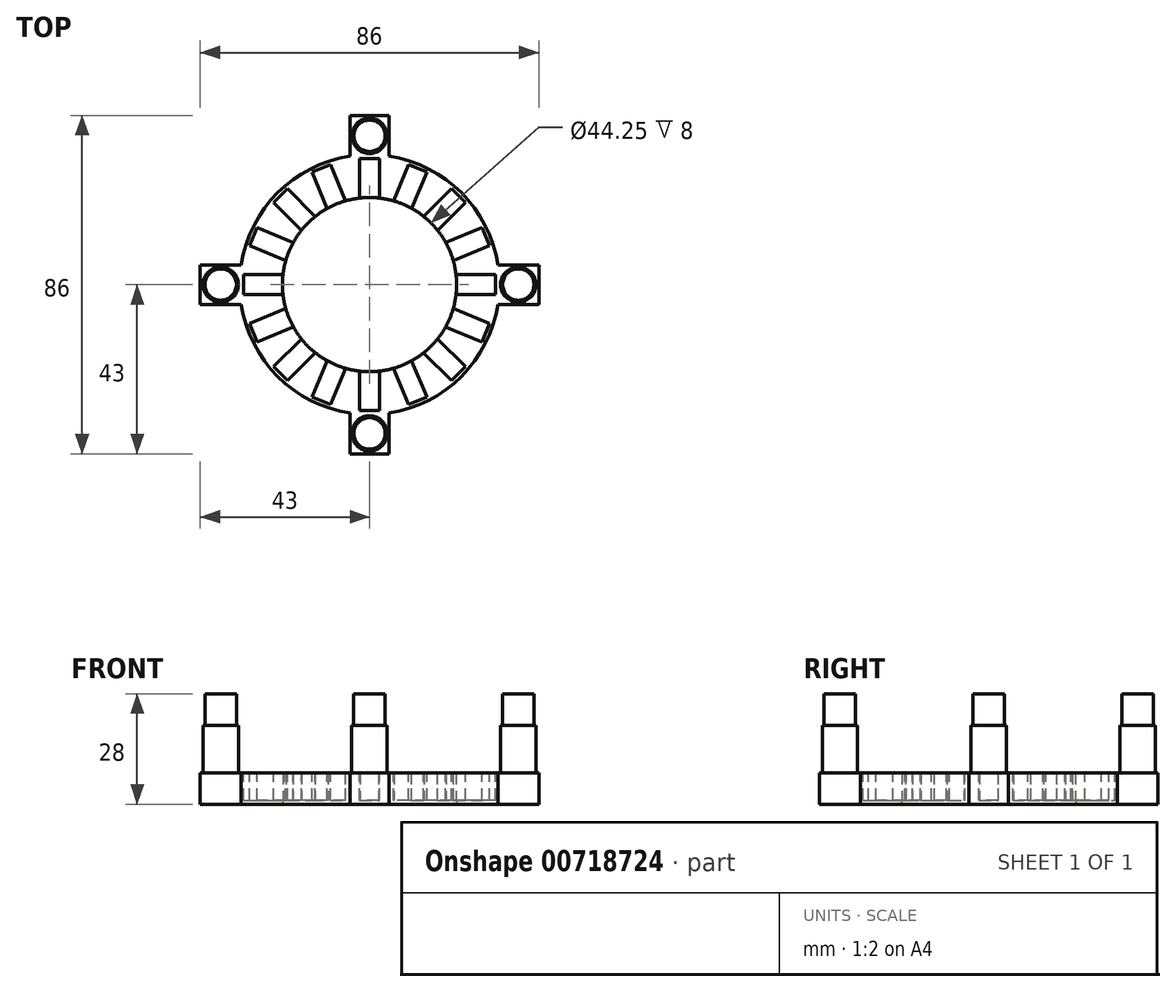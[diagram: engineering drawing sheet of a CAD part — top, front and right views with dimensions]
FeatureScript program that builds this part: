
annotation { "Feature Type Name" : "Feature", "Feature Type Description" : "" }
export const myFeature = defineFeature(function(context is Context, id is Id, definition is map)
    precondition{}
    {
        {
            var Q0;
            Q0=qCreatedBy(makeId("Front.planeOp"),FACE);
            var sketch = newSketch(context, id + "F0", { "sketchPlane" : qUnion([Q0])});
            skLineSegment(sketch, "E0", {"start": v(0, 0) * mm, "end": v(0, 8) * mm});
            skLineSegment(sketch, "E1", {"start": v(0, 8) * mm, "end": v(33, 8) * mm});
            skLineSegment(sketch, "E2", {"start": v(33, 8) * mm, "end": v(33, 0) * mm});
            skLineSegment(sketch, "E3", {"start": v(33, 0) * mm, "end": v(0, 0) * mm});
            skSolve(sketch);
        }
        {
            var Q0;
            Q0=qSketchRegion(id+"F0",true);
            var Q1;
            Q1=sQuery(id+"F0.wireOp",EDGE,"E0");
            revolve(context, id + "F1", {"surfaceOperationType" : NewSurfaceOperationType.NEW, "entities" : qUnion([Q0]), "axis" : qUnion([Q1]), "revolveType" : RevolveType.FULL});
        }
        {
            var Q0;
            Q0=qCreatedBy(makeId("Top.planeOp"),FACE);
            var sketch = newSketch(context, id + "F2", { "sketchPlane" : qUnion([Q0])});
            skCircle(sketch, "E4", {"center": v(0, 0) * mm, "radius": 22.12 * mm});
            skSolve(sketch);
        }
        {
            var Q0;
            Q0=qSketchRegion(id+"F2",true);
            extrude(context, id + "F3", {"entities" : qUnion([Q0]), "operationType" : NewBodyOperationType.REMOVE, "depth" : 25 * mm, "offsetDistance" : 25 * mm});
        }
        {
            var Q0;
            Q0=makeQuery(id+"F1.opRevolve","SWEPT_FACE",FACE,{"disambiguationData":[OSD([sQuery(id+"F0.wireOp",EDGE,"E1")])]});
            var sketch = newSketch(context, id + "F4", { "sketchPlane" : qUnion([Q0])});
            skLineSegment(sketch, "E5", {"start": v(0, 0) * mm, "end": v(0, 22) * mm});
            skLineSegment(sketch, "E6", {"start": v(0, 22) * mm, "end": v(-2.5, 22) * mm});
            skLineSegment(sketch, "E7", {"start": v(-2.5, 22) * mm, "end": v(-2.5, 32) * mm});
            skLineSegment(sketch, "E8", {"start": v(-2.5, 32) * mm, "end": v(2.5, 32) * mm});
            skLineSegment(sketch, "E9", {"start": v(2.5, 32) * mm, "end": v(2.5, 22) * mm});
            skLineSegment(sketch, "E10", {"start": v(2.5, 22) * mm, "end": v(0, 22) * mm});
            skLineSegment(sketch, "E11.1.0", {"start": v(-10.73, 19.37) * mm, "end": v(-14.56, 28.6) * mm});
            skLineSegment(sketch, "E11.1.1", {"start": v(-14.56, 28.6) * mm, "end": v(-9.94, 30.52) * mm});
            skLineSegment(sketch, "E11.1.2", {"start": v(-9.94, 30.52) * mm, "end": v(-6.1, 21.28) * mm});
            skLineSegment(sketch, "E11.1.3", {"start": v(-6.1, 21.28) * mm, "end": v(-8.42, 20.33) * mm});
            skLineSegment(sketch, "E11.1.4", {"start": v(-8.42, 20.33) * mm, "end": v(-10.73, 19.37) * mm});
            skLineSegment(sketch, "E11.2.0", {"start": v(-17.32, 13.79) * mm, "end": v(-24.4, 20.86) * mm});
            skLineSegment(sketch, "E11.2.1", {"start": v(-24.4, 20.86) * mm, "end": v(-20.86, 24.4) * mm});
            skLineSegment(sketch, "E11.2.2", {"start": v(-20.86, 24.4) * mm, "end": v(-13.79, 17.32) * mm});
            skLineSegment(sketch, "E11.2.3", {"start": v(-13.79, 17.32) * mm, "end": v(-15.56, 15.56) * mm});
            skLineSegment(sketch, "E11.2.4", {"start": v(-15.56, 15.56) * mm, "end": v(-17.32, 13.79) * mm});
            skPoint(sketch, "E11.center", {"position": v(0, 0) * mm});
            skLineSegment(sketch, "E12.1.3.0", {"start": v(-21.28, 6.1) * mm, "end": v(-30.52, 9.94) * mm});
            skLineSegment(sketch, "E12.3.3.0", {"start": v(-30.52, 9.94) * mm, "end": v(-28.6, 14.56) * mm});
            skLineSegment(sketch, "E12.6.3.0", {"start": v(-28.6, 14.56) * mm, "end": v(-19.37, 10.73) * mm});
            skLineSegment(sketch, "E12.9.3.0", {"start": v(-19.37, 10.73) * mm, "end": v(-20.33, 8.42) * mm});
            skLineSegment(sketch, "E12.12.3.0", {"start": v(-20.33, 8.42) * mm, "end": v(-21.28, 6.1) * mm});
            skLineSegment(sketch, "E12.1.4.0", {"start": v(-22, -2.5) * mm, "end": v(-32, -2.5) * mm});
            skLineSegment(sketch, "E12.3.4.0", {"start": v(-32, -2.5) * mm, "end": v(-32, 2.5) * mm});
            skLineSegment(sketch, "E12.6.4.0", {"start": v(-32, 2.5) * mm, "end": v(-22, 2.5) * mm});
            skLineSegment(sketch, "E12.9.4.0", {"start": v(-22, 2.5) * mm, "end": v(-22, 0) * mm});
            skLineSegment(sketch, "E12.12.4.0", {"start": v(-22, 0) * mm, "end": v(-22, -2.5) * mm});
            skLineSegment(sketch, "E12.1.5.0", {"start": v(-19.37, -10.73) * mm, "end": v(-28.6, -14.56) * mm});
            skLineSegment(sketch, "E12.3.5.0", {"start": v(-28.6, -14.56) * mm, "end": v(-30.52, -9.94) * mm});
            skLineSegment(sketch, "E12.6.5.0", {"start": v(-30.52, -9.94) * mm, "end": v(-21.28, -6.1) * mm});
            skLineSegment(sketch, "E12.9.5.0", {"start": v(-21.28, -6.1) * mm, "end": v(-20.33, -8.42) * mm});
            skLineSegment(sketch, "E12.12.5.0", {"start": v(-20.33, -8.42) * mm, "end": v(-19.37, -10.73) * mm});
            skLineSegment(sketch, "E12.1.6.0", {"start": v(-13.79, -17.32) * mm, "end": v(-20.86, -24.4) * mm});
            skLineSegment(sketch, "E12.3.6.0", {"start": v(-20.86, -24.4) * mm, "end": v(-24.4, -20.86) * mm});
            skLineSegment(sketch, "E12.6.6.0", {"start": v(-24.4, -20.86) * mm, "end": v(-17.32, -13.79) * mm});
            skLineSegment(sketch, "E12.9.6.0", {"start": v(-17.32, -13.79) * mm, "end": v(-15.56, -15.56) * mm});
            skLineSegment(sketch, "E12.12.6.0", {"start": v(-15.56, -15.56) * mm, "end": v(-13.79, -17.32) * mm});
            skLineSegment(sketch, "E12.1.7.0", {"start": v(-6.1, -21.28) * mm, "end": v(-9.94, -30.52) * mm});
            skLineSegment(sketch, "E12.3.7.0", {"start": v(-9.94, -30.52) * mm, "end": v(-14.56, -28.6) * mm});
            skLineSegment(sketch, "E12.6.7.0", {"start": v(-14.56, -28.6) * mm, "end": v(-10.73, -19.37) * mm});
            skLineSegment(sketch, "E12.9.7.0", {"start": v(-10.73, -19.37) * mm, "end": v(-8.42, -20.33) * mm});
            skLineSegment(sketch, "E12.12.7.0", {"start": v(-8.42, -20.33) * mm, "end": v(-6.1, -21.28) * mm});
            skLineSegment(sketch, "E12.1.8.0", {"start": v(2.5, -22) * mm, "end": v(2.5, -32) * mm});
            skLineSegment(sketch, "E12.3.8.0", {"start": v(2.5, -32) * mm, "end": v(-2.5, -32) * mm});
            skLineSegment(sketch, "E12.6.8.0", {"start": v(-2.5, -32) * mm, "end": v(-2.5, -22) * mm});
            skLineSegment(sketch, "E12.9.8.0", {"start": v(-2.5, -22) * mm, "end": v(0, -22) * mm});
            skLineSegment(sketch, "E12.12.8.0", {"start": v(0, -22) * mm, "end": v(2.5, -22) * mm});
            skLineSegment(sketch, "E12.1.9.0", {"start": v(10.73, -19.37) * mm, "end": v(14.56, -28.6) * mm});
            skLineSegment(sketch, "E12.3.9.0", {"start": v(14.56, -28.6) * mm, "end": v(9.94, -30.52) * mm});
            skLineSegment(sketch, "E12.6.9.0", {"start": v(9.94, -30.52) * mm, "end": v(6.1, -21.28) * mm});
            skLineSegment(sketch, "E12.9.9.0", {"start": v(6.1, -21.28) * mm, "end": v(8.42, -20.33) * mm});
            skLineSegment(sketch, "E12.12.9.0", {"start": v(8.42, -20.33) * mm, "end": v(10.73, -19.37) * mm});
            skLineSegment(sketch, "E12.1.10.0", {"start": v(17.32, -13.79) * mm, "end": v(24.4, -20.86) * mm});
            skLineSegment(sketch, "E12.3.10.0", {"start": v(24.4, -20.86) * mm, "end": v(20.86, -24.4) * mm});
            skLineSegment(sketch, "E12.6.10.0", {"start": v(20.86, -24.4) * mm, "end": v(13.79, -17.32) * mm});
            skLineSegment(sketch, "E12.9.10.0", {"start": v(13.79, -17.32) * mm, "end": v(15.56, -15.56) * mm});
            skLineSegment(sketch, "E12.12.10.0", {"start": v(15.56, -15.56) * mm, "end": v(17.32, -13.79) * mm});
            skLineSegment(sketch, "E12.1.11.0", {"start": v(21.28, -6.1) * mm, "end": v(30.52, -9.94) * mm});
            skLineSegment(sketch, "E12.3.11.0", {"start": v(30.52, -9.94) * mm, "end": v(28.6, -14.56) * mm});
            skLineSegment(sketch, "E12.6.11.0", {"start": v(28.6, -14.56) * mm, "end": v(19.37, -10.73) * mm});
            skLineSegment(sketch, "E12.9.11.0", {"start": v(19.37, -10.73) * mm, "end": v(20.33, -8.42) * mm});
            skLineSegment(sketch, "E12.12.11.0", {"start": v(20.33, -8.42) * mm, "end": v(21.28, -6.1) * mm});
            skLineSegment(sketch, "E12.1.12.0", {"start": v(22, 2.5) * mm, "end": v(32, 2.5) * mm});
            skLineSegment(sketch, "E12.3.12.0", {"start": v(32, 2.5) * mm, "end": v(32, -2.5) * mm});
            skLineSegment(sketch, "E12.6.12.0", {"start": v(32, -2.5) * mm, "end": v(22, -2.5) * mm});
            skLineSegment(sketch, "E12.9.12.0", {"start": v(22, -2.5) * mm, "end": v(22, 0) * mm});
            skLineSegment(sketch, "E12.12.12.0", {"start": v(22, 0) * mm, "end": v(22, 2.5) * mm});
            skLineSegment(sketch, "E12.1.13.0", {"start": v(19.37, 10.73) * mm, "end": v(28.6, 14.56) * mm});
            skLineSegment(sketch, "E12.3.13.0", {"start": v(28.6, 14.56) * mm, "end": v(30.52, 9.94) * mm});
            skLineSegment(sketch, "E12.6.13.0", {"start": v(30.52, 9.94) * mm, "end": v(21.28, 6.1) * mm});
            skLineSegment(sketch, "E12.9.13.0", {"start": v(21.28, 6.1) * mm, "end": v(20.33, 8.42) * mm});
            skLineSegment(sketch, "E12.12.13.0", {"start": v(20.33, 8.42) * mm, "end": v(19.37, 10.73) * mm});
            skLineSegment(sketch, "E12.1.14.0", {"start": v(13.79, 17.32) * mm, "end": v(20.86, 24.4) * mm});
            skLineSegment(sketch, "E12.3.14.0", {"start": v(20.86, 24.4) * mm, "end": v(24.4, 20.86) * mm});
            skLineSegment(sketch, "E12.6.14.0", {"start": v(24.4, 20.86) * mm, "end": v(17.32, 13.79) * mm});
            skLineSegment(sketch, "E12.9.14.0", {"start": v(17.32, 13.79) * mm, "end": v(15.56, 15.56) * mm});
            skLineSegment(sketch, "E12.12.14.0", {"start": v(15.56, 15.56) * mm, "end": v(13.79, 17.32) * mm});
            skLineSegment(sketch, "E12.1.15.0", {"start": v(6.1, 21.28) * mm, "end": v(9.94, 30.52) * mm});
            skLineSegment(sketch, "E12.3.15.0", {"start": v(9.94, 30.52) * mm, "end": v(14.56, 28.6) * mm});
            skLineSegment(sketch, "E12.6.15.0", {"start": v(14.56, 28.6) * mm, "end": v(10.73, 19.37) * mm});
            skLineSegment(sketch, "E12.9.15.0", {"start": v(10.73, 19.37) * mm, "end": v(8.42, 20.33) * mm});
            skLineSegment(sketch, "E12.12.15.0", {"start": v(8.42, 20.33) * mm, "end": v(6.1, 21.28) * mm});
            skSolve(sketch);
        }
        {
            var Q0;
            Q0=qSketchRegion(id+"F4",true);
            extrude(context, id + "F5", {"entities" : qUnion([Q0]), "operationType" : NewBodyOperationType.REMOVE, "oppositeDirection" : true, "depth" : 7 * mm, "offsetDistance" : 25 * mm});
        }
        {
            var Q0;
            Q0=qCreatedBy(makeId("Top.planeOp"),FACE);
            var sketch = newSketch(context, id + "F6", { "sketchPlane" : qUnion([Q0])});
            skLineSegment(sketch, "E13", {"start": v(0, 0) * mm, "end": v(0, 8) * mm});
            skLineSegment(sketch, "E14", {"start": v(43, 0) * mm, "end": v(43, -5) * mm});
            skLineSegment(sketch, "E15", {"start": v(43, -5) * mm, "end": v(32.62, -5) * mm});
            skLineSegment(sketch, "E16", {"start": v(43, 0) * mm, "end": v(43, 5) * mm});
            skLineSegment(sketch, "E17", {"start": v(43, 5) * mm, "end": v(32.62, 5) * mm});
            skLineSegment(sketch, "E18.1.0", {"start": v(5, 43) * mm, "end": v(5, 32.62) * mm});
            skLineSegment(sketch, "E18.1.1", {"start": v(0, 43) * mm, "end": v(5, 43) * mm});
            skLineSegment(sketch, "E18.1.2", {"start": v(0, 43) * mm, "end": v(-5, 43) * mm});
            skLineSegment(sketch, "E18.1.3", {"start": v(-5, 43) * mm, "end": v(-5, 32.62) * mm});
            skLineSegment(sketch, "E18.2.0", {"start": v(-43, 5) * mm, "end": v(-32.62, 5) * mm});
            skLineSegment(sketch, "E18.2.1", {"start": v(-43, 0) * mm, "end": v(-43, 5) * mm});
            skLineSegment(sketch, "E18.2.2", {"start": v(-43, 0) * mm, "end": v(-43, -5) * mm});
            skLineSegment(sketch, "E18.2.3", {"start": v(-43, -5) * mm, "end": v(-32.62, -5) * mm});
            skLineSegment(sketch, "E18.3.0", {"start": v(-5, -43) * mm, "end": v(-5, -32.62) * mm});
            skLineSegment(sketch, "E18.3.1", {"start": v(0, -43) * mm, "end": v(-5, -43) * mm});
            skLineSegment(sketch, "E18.3.2", {"start": v(0, -43) * mm, "end": v(5, -43) * mm});
            skLineSegment(sketch, "E18.3.3", {"start": v(5, -43) * mm, "end": v(5, -32.62) * mm});
            skPoint(sketch, "E18.center", {"position": v(0, 0) * mm});
            skLineSegment(sketch, "E19", {"start": v(32.62, 5) * mm, "end": v(32.62, -5) * mm});
            skLineSegment(sketch, "E20", {"start": v(5, 32.62) * mm, "end": v(-5, 32.62) * mm});
            skLineSegment(sketch, "E21", {"start": v(-32.62, 5) * mm, "end": v(-32.62, -5) * mm});
            skLineSegment(sketch, "E22", {"start": v(-5, -32.62) * mm, "end": v(5, -32.62) * mm});
            skSolve(sketch);
        }
        {
            var Q0;
            Q0=qSketchRegion(id+"F6",true);
            extrude(context, id + "F7", {"entities" : qUnion([Q0]), "operationType" : NewBodyOperationType.ADD, "depth" : 8 * mm, "offsetDistance" : 25 * mm});
        }
        {
            var Q0;
            Q0=makeQuery(id+"F7.boolean.opBoolean","MERGE",FACE,{"derivedFrom":[makeQuery(id+"F1.opRevolve","SWEPT_FACE",FACE,{"disambiguationData":[OSD([sQuery(id+"F0.wireOp",EDGE,"E1")])]}),makeQuery(id+"F7.opExtrude","CAP_FACE",FACE,{"disambiguationData":[OSD([sQuery(id+"F6.wireOp",EDGE,"E14"),sQuery(id+"F6.wireOp",EDGE,"E15"),sQuery(id+"F6.wireOp",EDGE,"E16"),sQuery(id+"F6.wireOp",EDGE,"E17"),sQuery(id+"F6.wireOp",EDGE,"E19")])],"isStart":false}),makeQuery(id+"F7.opExtrude","CAP_FACE",FACE,{"disambiguationData":[OSD([sQuery(id+"F6.wireOp",EDGE,"E18.1.0"),sQuery(id+"F6.wireOp",EDGE,"E18.1.1"),sQuery(id+"F6.wireOp",EDGE,"E18.1.2"),sQuery(id+"F6.wireOp",EDGE,"E18.1.3"),sQuery(id+"F6.wireOp",EDGE,"E20")])],"isStart":false}),makeQuery(id+"F7.opExtrude","CAP_FACE",FACE,{"disambiguationData":[OSD([sQuery(id+"F6.wireOp",EDGE,"E18.2.0"),sQuery(id+"F6.wireOp",EDGE,"E18.2.1"),sQuery(id+"F6.wireOp",EDGE,"E18.2.2"),sQuery(id+"F6.wireOp",EDGE,"E18.2.3"),sQuery(id+"F6.wireOp",EDGE,"E21")])],"isStart":false}),makeQuery(id+"F7.opExtrude","CAP_FACE",FACE,{"disambiguationData":[OSD([sQuery(id+"F6.wireOp",EDGE,"E18.3.0"),sQuery(id+"F6.wireOp",EDGE,"E18.3.1"),sQuery(id+"F6.wireOp",EDGE,"E18.3.2"),sQuery(id+"F6.wireOp",EDGE,"E18.3.3"),sQuery(id+"F6.wireOp",EDGE,"E22")])],"isStart":false})]});
            var sketch = newSketch(context, id + "F8", { "sketchPlane" : qUnion([Q0])});
            skPoint(sketch, "E23", {"position": v(0, 38.1) * mm});
            skPoint(sketch, "E24", {"position": v(37.8, 0) * mm});
            skPoint(sketch, "E24.positionSnap0", {"position": v(37.8, 5) * mm});
            skCircle(sketch, "E25", {"center": v(37.8, 0) * mm, "radius": 4 * mm});
            skCircle(sketch, "E26.1.0", {"center": v(0, 37.8) * mm, "radius": 4 * mm});
            skCircle(sketch, "E26.2.0", {"center": v(-37.8, 0) * mm, "radius": 4 * mm});
            skCircle(sketch, "E26.3.0", {"center": v(0, -37.8) * mm, "radius": 4 * mm});
            skPoint(sketch, "E26.center", {"position": v(0, 0) * mm});
            skSolve(sketch);
        }
        {
            var Q0;
            Q0=makeQuery(id+"F8.imprint","IMPRINT",FACE,{"disambiguationData":[TD([[makeQuery(id+"F8.imprint","IMPRINT",EDGE,{"derivedFrom":sQuery(id+"F8.wireOp",EDGE,"E26.1.0")}),1.0]])]});
            var Q1;
            Q1=makeQuery(id+"F8.imprint","IMPRINT",FACE,{"disambiguationData":[TD([[makeQuery(id+"F8.imprint","IMPRINT",EDGE,{"derivedFrom":sQuery(id+"F8.wireOp",EDGE,"E25")}),1.0]])]});
            var Q2;
            Q2=makeQuery(id+"F8.imprint","IMPRINT",FACE,{"disambiguationData":[TD([[makeQuery(id+"F8.imprint","IMPRINT",EDGE,{"derivedFrom":sQuery(id+"F8.wireOp",EDGE,"E26.2.0")}),1.0]])]});
            var Q3;
            Q3=makeQuery(id+"F8.imprint","IMPRINT",FACE,{"disambiguationData":[TD([[makeQuery(id+"F8.imprint","IMPRINT",EDGE,{"derivedFrom":sQuery(id+"F8.wireOp",EDGE,"E26.3.0")}),1.0]])]});
            extrude(context, id + "F9", {"entities" : qUnion([Q0, Q1, Q2, Q3]), "operationType" : NewBodyOperationType.REMOVE, "oppositeDirection" : true, "depth" : 25 * mm, "offsetDistance" : 25 * mm});
        }
        {
            var Q0;
            Q0=makeQuery(id+"F7.boolean.opBoolean","MERGE",FACE,{"derivedFrom":[makeQuery(id+"F1.opRevolve","SWEPT_FACE",FACE,{"disambiguationData":[OSD([sQuery(id+"F0.wireOp",EDGE,"E3")])]}),makeQuery(id+"F7.opExtrude","CAP_FACE",FACE,{"disambiguationData":[OSD([sQuery(id+"F6.wireOp",EDGE,"E14"),sQuery(id+"F6.wireOp",EDGE,"E15"),sQuery(id+"F6.wireOp",EDGE,"E16"),sQuery(id+"F6.wireOp",EDGE,"E17"),sQuery(id+"F6.wireOp",EDGE,"E19")])],"isStart":true}),makeQuery(id+"F7.opExtrude","CAP_FACE",FACE,{"disambiguationData":[OSD([sQuery(id+"F6.wireOp",EDGE,"E18.1.0"),sQuery(id+"F6.wireOp",EDGE,"E18.1.1"),sQuery(id+"F6.wireOp",EDGE,"E18.1.2"),sQuery(id+"F6.wireOp",EDGE,"E18.1.3"),sQuery(id+"F6.wireOp",EDGE,"E20")])],"isStart":true}),makeQuery(id+"F7.opExtrude","CAP_FACE",FACE,{"disambiguationData":[OSD([sQuery(id+"F6.wireOp",EDGE,"E18.2.0"),sQuery(id+"F6.wireOp",EDGE,"E18.2.1"),sQuery(id+"F6.wireOp",EDGE,"E18.2.2"),sQuery(id+"F6.wireOp",EDGE,"E18.2.3"),sQuery(id+"F6.wireOp",EDGE,"E21")])],"isStart":true}),makeQuery(id+"F7.opExtrude","CAP_FACE",FACE,{"disambiguationData":[OSD([sQuery(id+"F6.wireOp",EDGE,"E18.3.0"),sQuery(id+"F6.wireOp",EDGE,"E18.3.1"),sQuery(id+"F6.wireOp",EDGE,"E18.3.2"),sQuery(id+"F6.wireOp",EDGE,"E18.3.3"),sQuery(id+"F6.wireOp",EDGE,"E22")])],"isStart":true})]});
            var sketch = newSketch(context, id + "F10", { "sketchPlane" : qUnion([Q0])});
            skLineSegment(sketch, "E27", {"start": v(0, -37.8) * mm, "end": v(0, 37.8) * mm});
            skLineSegment(sketch, "E28", {"start": v(37.8, 0) * mm, "end": v(-37.8, 0) * mm});
            skLineSegment(sketch, "E29", {"start": v(0, 37.8) * mm, "end": v(0, 43) * mm});
            skLineSegment(sketch, "E30", {"start": v(0, -37.8) * mm, "end": v(0, -43) * mm});
            skPoint(sketch, "E31", {"position": v(0, 22.12) * mm});
            skPoint(sketch, "E32", {"position": v(0, -22.12) * mm});
            skCircle(sketch, "E33", {"center": v(0, -37.8) * mm, "radius": 4.5 * mm});
            skCircle(sketch, "E34.1.0", {"center": v(37.8, 0) * mm, "radius": 4.5 * mm});
            skCircle(sketch, "E34.2.0", {"center": v(0, 37.8) * mm, "radius": 4.5 * mm});
            skCircle(sketch, "E34.3.0", {"center": v(-37.8, 0) * mm, "radius": 4.5 * mm});
            skPoint(sketch, "E34.center", {"position": v(0, 0) * mm});
            skSolve(sketch);
        }
        {
            var Q0;
            {var subQ0=sQuery(id+"F10.wireOp",EDGE,"E30");var subQ1=sQuery(id+"F10.wireOp",EDGE,"E27");var subQ2=makeQuery(id+"F10.imprint","INTERSECT",VERTEX,{"derivedFrom":[subQ1,subQ0]});Q0=makeQuery(id+"F10.imprint","IMPRINT",FACE,{"disambiguationData":[TD([[makeQuery(id+"F10.imprint","IMPRINT",EDGE,{"disambiguationData":[TD([[subQ2,-1.0]])],"derivedFrom":subQ1}),1.0]])]});}
            var Q1;
            {var subQ0=sQuery(id+"F10.wireOp",EDGE,"E30");var subQ1=sQuery(id+"F10.wireOp",EDGE,"E27");var subQ2=makeQuery(id+"F10.imprint","INTERSECT",VERTEX,{"derivedFrom":[subQ1,subQ0]});Q1=makeQuery(id+"F10.imprint","IMPRINT",FACE,{"disambiguationData":[TD([[makeQuery(id+"F10.imprint","IMPRINT",EDGE,{"disambiguationData":[TD([[subQ2,-1.0]])],"derivedFrom":subQ1}),-1.0]])]});}
            var Q2;
            Q2=makeQuery(id+"F10.imprint","IMPRINT",FACE,{"disambiguationData":[TD([[makeQuery(id+"F10.imprint","IMPRINT",EDGE,{"derivedFrom":makeQuery(id+"F9.boolean.opBoolean","INTERSECT",EDGE,{"derivedFrom":[makeQuery(id+"F7.boolean.opBoolean","MERGE",FACE,{"derivedFrom":[makeQuery(id+"F1.opRevolve","SWEPT_FACE",FACE,{"disambiguationData":[OSD([sQuery(id+"F0.wireOp",EDGE,"E3")])]}),makeQuery(id+"F7.opExtrude","CAP_FACE",FACE,{"disambiguationData":[OSD([sQuery(id+"F6.wireOp",EDGE,"E14"),sQuery(id+"F6.wireOp",EDGE,"E15"),sQuery(id+"F6.wireOp",EDGE,"E16"),sQuery(id+"F6.wireOp",EDGE,"E17"),sQuery(id+"F6.wireOp",EDGE,"E19")])],"isStart":true}),makeQuery(id+"F7.opExtrude","CAP_FACE",FACE,{"disambiguationData":[OSD([sQuery(id+"F6.wireOp",EDGE,"E18.1.0"),sQuery(id+"F6.wireOp",EDGE,"E18.1.1"),sQuery(id+"F6.wireOp",EDGE,"E18.1.2"),sQuery(id+"F6.wireOp",EDGE,"E18.1.3"),sQuery(id+"F6.wireOp",EDGE,"E20")])],"isStart":true}),makeQuery(id+"F7.opExtrude","CAP_FACE",FACE,{"disambiguationData":[OSD([sQuery(id+"F6.wireOp",EDGE,"E18.2.0"),sQuery(id+"F6.wireOp",EDGE,"E18.2.1"),sQuery(id+"F6.wireOp",EDGE,"E18.2.2"),sQuery(id+"F6.wireOp",EDGE,"E18.2.3"),sQuery(id+"F6.wireOp",EDGE,"E21")])],"isStart":true}),makeQuery(id+"F7.opExtrude","CAP_FACE",FACE,{"disambiguationData":[OSD([sQuery(id+"F6.wireOp",EDGE,"E18.3.0"),sQuery(id+"F6.wireOp",EDGE,"E18.3.1"),sQuery(id+"F6.wireOp",EDGE,"E18.3.2"),sQuery(id+"F6.wireOp",EDGE,"E18.3.3"),sQuery(id+"F6.wireOp",EDGE,"E22")])],"isStart":true})]}),makeQuery(id+"F9.opExtrude","SWEPT_FACE",FACE,{"disambiguationData":[OSD([sQuery(id+"F8.wireOp",EDGE,"E25")])]})]})}),-1.0]])]});
            var Q3;
            {var subQ0=sQuery(id+"F10.wireOp",EDGE,"E29");var subQ1=sQuery(id+"F10.wireOp",EDGE,"E27");var subQ2=makeQuery(id+"F10.imprint","INTERSECT",VERTEX,{"derivedFrom":[subQ1,subQ0]});Q3=makeQuery(id+"F10.imprint","IMPRINT",FACE,{"disambiguationData":[TD([[makeQuery(id+"F10.imprint","IMPRINT",EDGE,{"disambiguationData":[TD([[subQ2,1.0]])],"derivedFrom":subQ1}),1.0]])]});}
            var Q4;
            {var subQ0=sQuery(id+"F10.wireOp",EDGE,"E29");var subQ1=sQuery(id+"F10.wireOp",EDGE,"E27");var subQ2=makeQuery(id+"F10.imprint","INTERSECT",VERTEX,{"derivedFrom":[subQ1,subQ0]});Q4=makeQuery(id+"F10.imprint","IMPRINT",FACE,{"disambiguationData":[TD([[makeQuery(id+"F10.imprint","IMPRINT",EDGE,{"disambiguationData":[TD([[subQ2,1.0]])],"derivedFrom":subQ1}),-1.0]])]});}
            var Q5;
            Q5=makeQuery(id+"F10.imprint","IMPRINT",FACE,{"disambiguationData":[TD([[makeQuery(id+"F10.imprint","IMPRINT",EDGE,{"derivedFrom":sQuery(id+"F10.wireOp",EDGE,"E34.1.0")}),1.0]])]});
            var Q6;
            {var subQ0=sQuery(id+"F10.wireOp",EDGE,"E33");var subQ1=sQuery(id+"F10.wireOp",EDGE,"E27");var subQ2=makeQuery(id+"F10.imprint","INTERSECT",VERTEX,{"derivedFrom":[subQ1,subQ0]});Q6=makeQuery(id+"F10.imprint","IMPRINT",FACE,{"disambiguationData":[TD([[makeQuery(id+"F10.imprint","IMPRINT",EDGE,{"disambiguationData":[TD([[subQ2,1.0]])],"derivedFrom":subQ0}),1.0]])]});}
            var Q7;
            {var subQ0=sQuery(id+"F10.wireOp",EDGE,"E33");var subQ1=sQuery(id+"F10.wireOp",EDGE,"E27");var subQ2=makeQuery(id+"F10.imprint","INTERSECT",VERTEX,{"derivedFrom":[subQ1,subQ0]});Q7=makeQuery(id+"F10.imprint","IMPRINT",FACE,{"disambiguationData":[TD([[makeQuery(id+"F10.imprint","IMPRINT",EDGE,{"disambiguationData":[TD([[subQ2,-1.0]])],"derivedFrom":subQ0}),1.0]])]});}
            var Q8;
            Q8=makeQuery(id+"F10.imprint","IMPRINT",FACE,{"disambiguationData":[TD([[makeQuery(id+"F10.imprint","IMPRINT",EDGE,{"derivedFrom":sQuery(id+"F10.wireOp",EDGE,"E34.3.0")}),1.0]])]});
            var Q9;
            {var subQ0=sQuery(id+"F10.wireOp",EDGE,"E34.2.0");var subQ1=sQuery(id+"F10.wireOp",EDGE,"E27");var subQ2=makeQuery(id+"F10.imprint","INTERSECT",VERTEX,{"derivedFrom":[subQ1,subQ0]});Q9=makeQuery(id+"F10.imprint","IMPRINT",FACE,{"disambiguationData":[TD([[makeQuery(id+"F10.imprint","IMPRINT",EDGE,{"disambiguationData":[TD([[subQ2,1.0]])],"derivedFrom":subQ0}),1.0]])]});}
            var Q10;
            {var subQ0=sQuery(id+"F10.wireOp",EDGE,"E34.2.0");var subQ1=sQuery(id+"F10.wireOp",EDGE,"E27");var subQ2=makeQuery(id+"F10.imprint","INTERSECT",VERTEX,{"derivedFrom":[subQ1,subQ0]});Q10=makeQuery(id+"F10.imprint","IMPRINT",FACE,{"disambiguationData":[TD([[makeQuery(id+"F10.imprint","IMPRINT",EDGE,{"disambiguationData":[TD([[subQ2,-1.0]])],"derivedFrom":subQ0}),1.0]])]});}
            var Q11;
            Q11=makeQuery(id+"F10.imprint","IMPRINT",FACE,{"disambiguationData":[TD([[makeQuery(id+"F10.imprint","IMPRINT",EDGE,{"derivedFrom":makeQuery(id+"F9.boolean.opBoolean","INTERSECT",EDGE,{"derivedFrom":[makeQuery(id+"F7.boolean.opBoolean","MERGE",FACE,{"derivedFrom":[makeQuery(id+"F1.opRevolve","SWEPT_FACE",FACE,{"disambiguationData":[OSD([sQuery(id+"F0.wireOp",EDGE,"E3")])]}),makeQuery(id+"F7.opExtrude","CAP_FACE",FACE,{"disambiguationData":[OSD([sQuery(id+"F6.wireOp",EDGE,"E14"),sQuery(id+"F6.wireOp",EDGE,"E15"),sQuery(id+"F6.wireOp",EDGE,"E16"),sQuery(id+"F6.wireOp",EDGE,"E17"),sQuery(id+"F6.wireOp",EDGE,"E19")])],"isStart":true}),makeQuery(id+"F7.opExtrude","CAP_FACE",FACE,{"disambiguationData":[OSD([sQuery(id+"F6.wireOp",EDGE,"E18.1.0"),sQuery(id+"F6.wireOp",EDGE,"E18.1.1"),sQuery(id+"F6.wireOp",EDGE,"E18.1.2"),sQuery(id+"F6.wireOp",EDGE,"E18.1.3"),sQuery(id+"F6.wireOp",EDGE,"E20")])],"isStart":true}),makeQuery(id+"F7.opExtrude","CAP_FACE",FACE,{"disambiguationData":[OSD([sQuery(id+"F6.wireOp",EDGE,"E18.2.0"),sQuery(id+"F6.wireOp",EDGE,"E18.2.1"),sQuery(id+"F6.wireOp",EDGE,"E18.2.2"),sQuery(id+"F6.wireOp",EDGE,"E18.2.3"),sQuery(id+"F6.wireOp",EDGE,"E21")])],"isStart":true}),makeQuery(id+"F7.opExtrude","CAP_FACE",FACE,{"disambiguationData":[OSD([sQuery(id+"F6.wireOp",EDGE,"E18.3.0"),sQuery(id+"F6.wireOp",EDGE,"E18.3.1"),sQuery(id+"F6.wireOp",EDGE,"E18.3.2"),sQuery(id+"F6.wireOp",EDGE,"E18.3.3"),sQuery(id+"F6.wireOp",EDGE,"E22")])],"isStart":true})]}),makeQuery(id+"F9.opExtrude","SWEPT_FACE",FACE,{"disambiguationData":[OSD([sQuery(id+"F8.wireOp",EDGE,"E26.2.0")])]})]})}),-1.0]])]});
            extrude(context, id + "F11", {"entities" : qUnion([Q0, Q1, Q2, Q3, Q4, Q5, Q6, Q7, Q8, Q9, Q10, Q11]), "operationType" : NewBodyOperationType.ADD, "oppositeDirection" : true, "depth" : 20 * mm, "offsetDistance" : 25 * mm});
        }
        {
            var Q0;
            Q0=makeQuery(id+"F10.imprint","IMPRINT",FACE,{"disambiguationData":[TD([[makeQuery(id+"F10.imprint","IMPRINT",EDGE,{"derivedFrom":makeQuery(id+"F9.boolean.opBoolean","INTERSECT",EDGE,{"derivedFrom":[makeQuery(id+"F7.boolean.opBoolean","MERGE",FACE,{"derivedFrom":[makeQuery(id+"F1.opRevolve","SWEPT_FACE",FACE,{"disambiguationData":[OSD([sQuery(id+"F0.wireOp",EDGE,"E3")])]}),makeQuery(id+"F7.opExtrude","CAP_FACE",FACE,{"disambiguationData":[OSD([sQuery(id+"F6.wireOp",EDGE,"E14"),sQuery(id+"F6.wireOp",EDGE,"E15"),sQuery(id+"F6.wireOp",EDGE,"E16"),sQuery(id+"F6.wireOp",EDGE,"E17"),sQuery(id+"F6.wireOp",EDGE,"E19")])],"isStart":true}),makeQuery(id+"F7.opExtrude","CAP_FACE",FACE,{"disambiguationData":[OSD([sQuery(id+"F6.wireOp",EDGE,"E18.1.0"),sQuery(id+"F6.wireOp",EDGE,"E18.1.1"),sQuery(id+"F6.wireOp",EDGE,"E18.1.2"),sQuery(id+"F6.wireOp",EDGE,"E18.1.3"),sQuery(id+"F6.wireOp",EDGE,"E20")])],"isStart":true}),makeQuery(id+"F7.opExtrude","CAP_FACE",FACE,{"disambiguationData":[OSD([sQuery(id+"F6.wireOp",EDGE,"E18.2.0"),sQuery(id+"F6.wireOp",EDGE,"E18.2.1"),sQuery(id+"F6.wireOp",EDGE,"E18.2.2"),sQuery(id+"F6.wireOp",EDGE,"E18.2.3"),sQuery(id+"F6.wireOp",EDGE,"E21")])],"isStart":true}),makeQuery(id+"F7.opExtrude","CAP_FACE",FACE,{"disambiguationData":[OSD([sQuery(id+"F6.wireOp",EDGE,"E18.3.0"),sQuery(id+"F6.wireOp",EDGE,"E18.3.1"),sQuery(id+"F6.wireOp",EDGE,"E18.3.2"),sQuery(id+"F6.wireOp",EDGE,"E18.3.3"),sQuery(id+"F6.wireOp",EDGE,"E22")])],"isStart":true})]}),makeQuery(id+"F9.opExtrude","SWEPT_FACE",FACE,{"disambiguationData":[OSD([sQuery(id+"F8.wireOp",EDGE,"E26.2.0")])]})]})}),-1.0]])]});
            var Q1;
            {var subQ0=sQuery(id+"F10.wireOp",EDGE,"E29");var subQ1=sQuery(id+"F10.wireOp",EDGE,"E27");var subQ2=makeQuery(id+"F10.imprint","INTERSECT",VERTEX,{"derivedFrom":[subQ1,subQ0]});Q1=makeQuery(id+"F10.imprint","IMPRINT",FACE,{"disambiguationData":[TD([[makeQuery(id+"F10.imprint","IMPRINT",EDGE,{"disambiguationData":[TD([[subQ2,1.0]])],"derivedFrom":subQ1}),-1.0]])]});}
            var Q2;
            {var subQ0=sQuery(id+"F10.wireOp",EDGE,"E29");var subQ1=sQuery(id+"F10.wireOp",EDGE,"E27");var subQ2=makeQuery(id+"F10.imprint","INTERSECT",VERTEX,{"derivedFrom":[subQ1,subQ0]});Q2=makeQuery(id+"F10.imprint","IMPRINT",FACE,{"disambiguationData":[TD([[makeQuery(id+"F10.imprint","IMPRINT",EDGE,{"disambiguationData":[TD([[subQ2,1.0]])],"derivedFrom":subQ1}),1.0]])]});}
            var Q3;
            {var subQ0=sQuery(id+"F10.wireOp",EDGE,"E30");var subQ1=sQuery(id+"F10.wireOp",EDGE,"E27");var subQ2=makeQuery(id+"F10.imprint","INTERSECT",VERTEX,{"derivedFrom":[subQ1,subQ0]});Q3=makeQuery(id+"F10.imprint","IMPRINT",FACE,{"disambiguationData":[TD([[makeQuery(id+"F10.imprint","IMPRINT",EDGE,{"disambiguationData":[TD([[subQ2,-1.0]])],"derivedFrom":subQ1}),1.0]])]});}
            var Q4;
            {var subQ0=sQuery(id+"F10.wireOp",EDGE,"E30");var subQ1=sQuery(id+"F10.wireOp",EDGE,"E27");var subQ2=makeQuery(id+"F10.imprint","INTERSECT",VERTEX,{"derivedFrom":[subQ1,subQ0]});Q4=makeQuery(id+"F10.imprint","IMPRINT",FACE,{"disambiguationData":[TD([[makeQuery(id+"F10.imprint","IMPRINT",EDGE,{"disambiguationData":[TD([[subQ2,-1.0]])],"derivedFrom":subQ1}),-1.0]])]});}
            var Q5;
            Q5=makeQuery(id+"F10.imprint","IMPRINT",FACE,{"disambiguationData":[TD([[makeQuery(id+"F10.imprint","IMPRINT",EDGE,{"derivedFrom":makeQuery(id+"F9.boolean.opBoolean","INTERSECT",EDGE,{"derivedFrom":[makeQuery(id+"F7.boolean.opBoolean","MERGE",FACE,{"derivedFrom":[makeQuery(id+"F1.opRevolve","SWEPT_FACE",FACE,{"disambiguationData":[OSD([sQuery(id+"F0.wireOp",EDGE,"E3")])]}),makeQuery(id+"F7.opExtrude","CAP_FACE",FACE,{"disambiguationData":[OSD([sQuery(id+"F6.wireOp",EDGE,"E14"),sQuery(id+"F6.wireOp",EDGE,"E15"),sQuery(id+"F6.wireOp",EDGE,"E16"),sQuery(id+"F6.wireOp",EDGE,"E17"),sQuery(id+"F6.wireOp",EDGE,"E19")])],"isStart":true}),makeQuery(id+"F7.opExtrude","CAP_FACE",FACE,{"disambiguationData":[OSD([sQuery(id+"F6.wireOp",EDGE,"E18.1.0"),sQuery(id+"F6.wireOp",EDGE,"E18.1.1"),sQuery(id+"F6.wireOp",EDGE,"E18.1.2"),sQuery(id+"F6.wireOp",EDGE,"E18.1.3"),sQuery(id+"F6.wireOp",EDGE,"E20")])],"isStart":true}),makeQuery(id+"F7.opExtrude","CAP_FACE",FACE,{"disambiguationData":[OSD([sQuery(id+"F6.wireOp",EDGE,"E18.2.0"),sQuery(id+"F6.wireOp",EDGE,"E18.2.1"),sQuery(id+"F6.wireOp",EDGE,"E18.2.2"),sQuery(id+"F6.wireOp",EDGE,"E18.2.3"),sQuery(id+"F6.wireOp",EDGE,"E21")])],"isStart":true}),makeQuery(id+"F7.opExtrude","CAP_FACE",FACE,{"disambiguationData":[OSD([sQuery(id+"F6.wireOp",EDGE,"E18.3.0"),sQuery(id+"F6.wireOp",EDGE,"E18.3.1"),sQuery(id+"F6.wireOp",EDGE,"E18.3.2"),sQuery(id+"F6.wireOp",EDGE,"E18.3.3"),sQuery(id+"F6.wireOp",EDGE,"E22")])],"isStart":true})]}),makeQuery(id+"F9.opExtrude","SWEPT_FACE",FACE,{"disambiguationData":[OSD([sQuery(id+"F8.wireOp",EDGE,"E25")])]})]})}),-1.0]])]});
            extrude(context, id + "F12", {"entities" : qUnion([Q0, Q1, Q2, Q3, Q4, Q5]), "operationType" : NewBodyOperationType.ADD, "oppositeDirection" : true, "depth" : 28 * mm, "offsetDistance" : 25 * mm});
        }
    });
